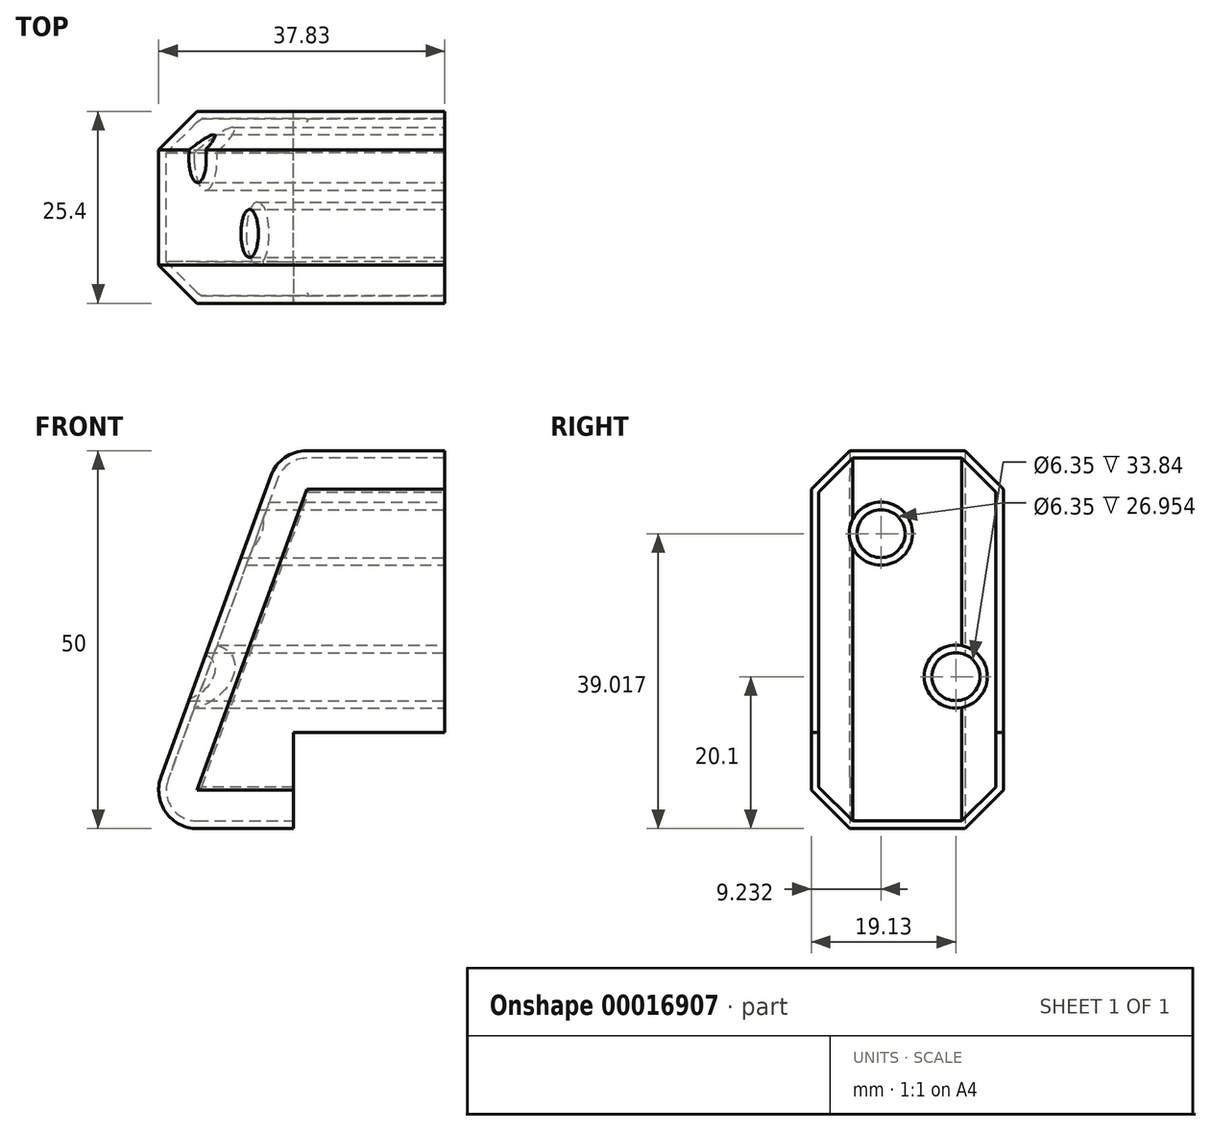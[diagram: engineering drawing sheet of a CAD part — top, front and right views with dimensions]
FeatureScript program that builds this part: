
annotation { "Feature Type Name" : "Feature", "Feature Type Description" : "" }
export const myFeature = defineFeature(function(context is Context, id is Id, definition is map)
    precondition{}
    {
        {
            var Q0;
            Q0=qCreatedBy(makeId("Front.planeOp"),FACE);
            var sketch = newSketch(context, id + "F0", { "sketchPlane" : qUnion([Q0])});
            skLineSegment(sketch, "E0", {"start": v(0, 0) * mm, "end": v(18.2, 50) * mm});
            skLineSegment(sketch, "E1", {"start": v(18.2, 50) * mm, "end": v(40, 50) * mm});
            skLineSegment(sketch, "E2", {"start": v(40, 50) * mm, "end": v(40, 12.7) * mm});
            skLineSegment(sketch, "E3", {"start": v(40, 12.7) * mm, "end": v(20, 12.7) * mm});
            skLineSegment(sketch, "E4", {"start": v(20, 12.7) * mm, "end": v(20, 0) * mm});
            skLineSegment(sketch, "E5", {"start": v(20, 0) * mm, "end": v(0, 0) * mm});
            skSolve(sketch);
        }
        {
            var Q0;
            Q0=makeQuery(id+"F0.imprint","IMPRINT",FACE,{"disambiguationData":[TD([[makeQuery(id+"F0.imprint","IMPRINT",EDGE,{"derivedFrom":sQuery(id+"F0.wireOp",EDGE,"E0")}),-1.0]])]});
            extrude(context, id + "F1", {"entities" : qUnion([Q0]), "depth" : 25.4 * mm});
        }
        {
            var Q0;
            Q0=makeQuery(id+"F1.opExtrude","SWEPT_FACE",FACE,{"disambiguationData":[OSD([sQuery(id+"F0.wireOp",EDGE,"E2")])]});
            var sketch = newSketch(context, id + "F2", { "sketchPlane" : qUnion([Q0])});
            skPoint(sketch, "E6", {"position": v(-16.17, 39.02) * mm});
            skPoint(sketch, "E7", {"position": v(-6.27, 20.1) * mm});
            skSolve(sketch);
        }
        {
            var Q0;
            Q0=sQuery(id+"F2.wireOp",VERTEX,"E6");
            var Q1;
            Q1=sQuery(id+"F2.wireOp",VERTEX,"E7");
            var Q2;
            Q2=makeQuery(id+"F1.opExtrude","SWEPT_BODY",BODY,{"disambiguationData":[OSD([sQuery(id+"F0.wireOp",EDGE,"E0"),sQuery(id+"F0.wireOp",EDGE,"E1"),sQuery(id+"F0.wireOp",EDGE,"E2"),sQuery(id+"F0.wireOp",EDGE,"E3"),sQuery(id+"F0.wireOp",EDGE,"E4"),sQuery(id+"F0.wireOp",EDGE,"E5")])]});
            hole(context, id + "F3", {"style" : HoleStyle.SIMPLE, "holeDiameter" : 6.35 * mm, "endStyle" : HoleEndStyle.THROUGH, "locations" : qUnion([Q0, Q1]), "scope" : qUnion([Q2])});
        }
        {
            var Q0;
            Q0=makeQuery(id+"F1.opExtrude","SWEPT_EDGE",EDGE,{"disambiguationData":[OSD([sQuery(id+"F0.wireOp",EDGE,"E0"),sQuery(id+"F0.wireOp",EDGE,"E5")])]});
            var Q1;
            Q1=makeQuery(id+"F1.opExtrude","SWEPT_EDGE",EDGE,{"disambiguationData":[OSD([sQuery(id+"F0.wireOp",EDGE,"E0"),sQuery(id+"F0.wireOp",EDGE,"E1")])]});
            fillet(context, id + "F4", {"entities" : qUnion([Q0, Q1]), "radius" : 5.08 * mm, "tangentPropagation" : true, "allowEdgeOverflow" : false});
        }
        {
            var Q0;
            Q0=makeQuery(id+"F1.opExtrude","CAP_EDGE",EDGE,{"disambiguationData":[OSD([sQuery(id+"F0.wireOp",EDGE,"E0")])],"isStart":true});
            var Q1;
            Q1=makeQuery(id+"F1.opExtrude","CAP_EDGE",EDGE,{"disambiguationData":[OSD([sQuery(id+"F0.wireOp",EDGE,"E0")])],"isStart":false});
            chamfer(context, id + "F5", {"entities" : qUnion([Q0, Q1]), "width" : 5.08 * mm, "tangentPropagation" : true});
        }
        {
            var Q0;
            Q0=makeQuery(id+"F1.opExtrude","SWEPT_FACE",FACE,{"disambiguationData":[OSD([sQuery(id+"F0.wireOp",EDGE,"E2")])]});
            var Q1;
            Q1=makeQuery(id+"F1.opExtrude","SWEPT_FACE",FACE,{"disambiguationData":[OSD([sQuery(id+"F0.wireOp",EDGE,"E4")])]});
            var Q2;
            Q2=makeQuery(id+"F1.opExtrude","SWEPT_FACE",FACE,{"disambiguationData":[OSD([sQuery(id+"F0.wireOp",EDGE,"E3")])]});
            shell(context, id + "F6", {"entities" : qUnion([Q0, Q1, Q2]), "thickness" : 1 * mm});
        }
    });
